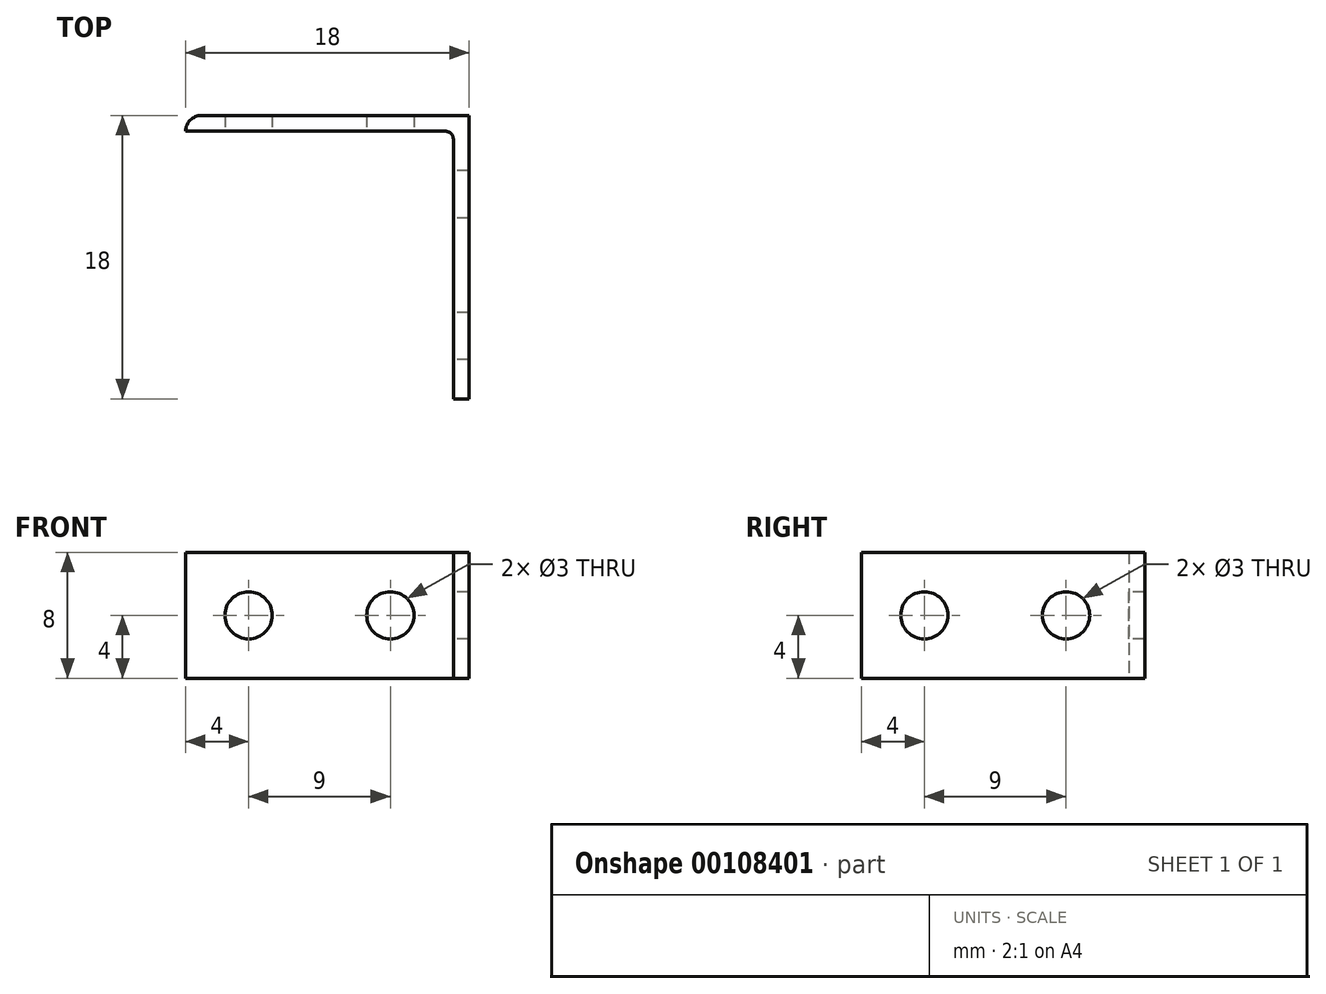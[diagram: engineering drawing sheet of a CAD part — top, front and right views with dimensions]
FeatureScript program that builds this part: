
annotation { "Feature Type Name" : "Feature", "Feature Type Description" : "" }
export const myFeature = defineFeature(function(context is Context, id is Id, definition is map)
    precondition{}
    {
        {
            var Q0;
            Q0=qCreatedBy(makeId("Top.planeOp"),FACE);
            var sketch = newSketch(context, id + "F0", { "sketchPlane" : qUnion([Q0])});
            skLineSegment(sketch, "E0.bottom", {"start": v(-0.5, 9) * mm, "end": v(0.5, 9) * mm});
            skLineSegment(sketch, "E0.top", {"start": v(-0.5, -9) * mm, "end": v(0.5, -9) * mm});
            skLineSegment(sketch, "E0.left", {"start": v(-0.5, 9) * mm, "end": v(-0.5, -9) * mm});
            skLineSegment(sketch, "E0.right", {"start": v(0.5, 9) * mm, "end": v(0.5, -9) * mm});
            skPoint(sketch, "E0.middle", {"position": v(0, 0) * mm});
            skLineSegment(sketch, "E1.bottom", {"start": v(0.5, 9) * mm, "end": v(-17.5, 9) * mm});
            skLineSegment(sketch, "E1.top", {"start": v(0.5, 8) * mm, "end": v(-17.5, 8) * mm});
            skLineSegment(sketch, "E1.left", {"start": v(0.5, 9) * mm, "end": v(0.5, 8) * mm});
            skLineSegment(sketch, "E1.right", {"start": v(-17.5, 9) * mm, "end": v(-17.5, 8) * mm});
            skSolve(sketch);
        }
        {
            var Q0;
            Q0 = qSketchRegion(id + "F0", true);
            extrude(context, id + "F1", {"entities" : qUnion([Q0]), "depth" : 8 * mm});
        }
        {
            var Q0;
            Q0=makeQuery(id+"F1.opExtrude","SWEPT_FACE",FACE,{"disambiguationData":[OSD([sQuery(id+"F0.wireOp",EDGE,"E0.left")])]});
            var sketch = newSketch(context, id + "F2", { "sketchPlane" : qUnion([Q0])});
            skLineSegment(sketch, "E2", {"start": v(9, 4) * mm, "end": v(5, 4) * mm});
            skPoint(sketch, "E2.endSnap0", {"position": v(9, 4) * mm});
            skCircle(sketch, "E3", {"center": v(5, 4) * mm, "radius": 1.5 * mm});
            skCircle(sketch, "E4.1.0.0", {"center": v(-4, 4) * mm, "radius": 1.5 * mm});
            skLineSegment(sketch, "E4.direction1", {"start": v(5, 4) * mm, "end": v(-4, 4) * mm, "construction": true});
            skSolve(sketch);
        }
        {
            var Q0;
            Q0=makeQuery(id+"F1.opExtrude","SWEPT_FACE",FACE,{"disambiguationData":[OSD([sQuery(id+"F0.wireOp",EDGE,"E1.top")])]});
            var sketch = newSketch(context, id + "F3", { "sketchPlane" : qUnion([Q0])});
            skLineSegment(sketch, "E5", {"start": v(-17.5, 4) * mm, "end": v(-13.5, 4) * mm});
            skCircle(sketch, "E6", {"center": v(-13.5, 4) * mm, "radius": 1.5 * mm});
            skCircle(sketch, "E7.1.0.0", {"center": v(-4.5, 4) * mm, "radius": 1.5 * mm});
            skLineSegment(sketch, "E7.direction1", {"start": v(-13.5, 4) * mm, "end": v(-4.5, 4) * mm, "construction": true});
            skSolve(sketch);
        }
        {
            var Q0;
            Q0 = qSketchRegion(id + "F3", true);
            extrude(context, id + "F4", {"entities" : qUnion([Q0]), "operationType" : NewBodyOperationType.REMOVE, "oppositeDirection" : true, "depth" : 25 * mm});
        }
        {
            var Q0;
            Q0 = qSketchRegion(id + "F2", true);
            extrude(context, id + "F5", {"entities" : qUnion([Q0]), "operationType" : NewBodyOperationType.REMOVE, "oppositeDirection" : true, "depth" : 25 * mm});
        }
        {
            var Q0;
            Q0=makeQuery(id+"F1.opExtrude","SWEPT_EDGE",EDGE,{"disambiguationData":[OSD([sQuery(id+"F0.wireOp",EDGE,"E1.bottom"),sQuery(id+"F0.wireOp",EDGE,"E1.left")])]});
            fillet(context, id + "F6", {"entities" : qUnion([Q0]), "radius" : 1 * mm, "tangentPropagation" : true, "allowEdgeOverflow" : false});
        }
        {
            var Q0;
            Q0=makeQuery(id+"F1.opExtrude","SWEPT_EDGE",EDGE,{"disambiguationData":[OSD([sQuery(id+"F0.wireOp",EDGE,"E0.left"),sQuery(id+"F0.wireOp",EDGE,"E1.top")])]});
            fillet(context, id + "F7", {"entities" : qUnion([Q0]), "radius" : .5 * mm, "tangentPropagation" : true, "allowEdgeOverflow" : false});
        }
    });
